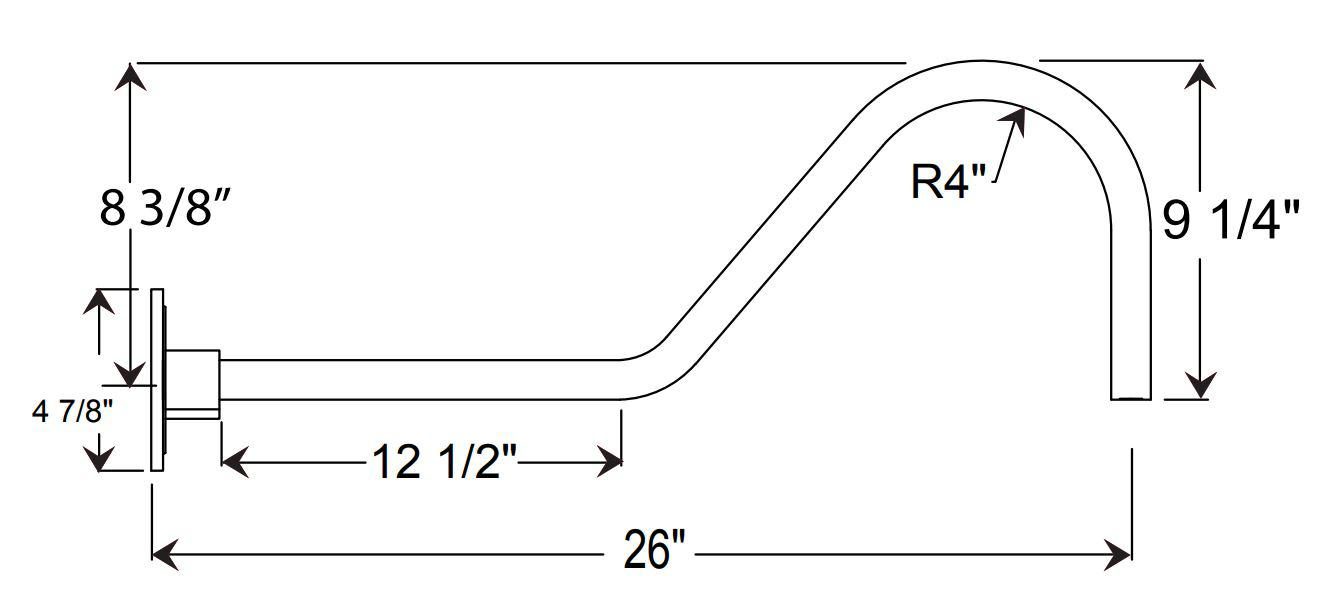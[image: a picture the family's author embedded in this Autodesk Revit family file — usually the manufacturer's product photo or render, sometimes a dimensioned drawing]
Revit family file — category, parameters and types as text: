
# Revit family: MILKCAN T(8,10,12,18)MB
name_source: partatom
category: Lighting Fixtures
units: mm (PartAtom-declared; Revit-internal decimal feet)

## family parameters
Always vertical = Yes
Cut with Voids When Loaded = No
Light Source = Yes
OmniClass Number = 23.80.70.00
OmniClass Title = Lighting
Part Type = Normal
Room Calculation Point = No
Round Connector Dimension = Use Diameter
Shared = No
Work Plane-Based = No

## types (4) — shared parameters
Body Colour = Spun aluminium
Body Material = body
CRI = >90
Color Filter = 16777215
Construction Material = Heavy Duty spun aluminum.
Default Elevation = 0' - 0"
Description = 120-277 Voltage
Dimming = 1%
Dimming Lamp Color Temperature Shift = <None>
Efficiency = 65-125 lumens per watt
Lamp = MB
Life = L70 50,000 hours
Load Classification = Lighting
Manufacturer = ANP Lighting
Photometric Web File = generic.ies
Power Factor = 1
Tilt Angle = 90.00°
URL = https://www.anplighting.com
Voltage = 277 V
Warranty = 5 year limited warranty

## per-type parameters (varying)
| type | Apparent Load | Fixture Diameter | Fixture Height | MCT10 | MCT12 | MCT18 | MCT8 | Wattage Comments | Weight |
| MCT08 | 100 VA | 0' - 8" | 0' - 5" | No | No | No | Yes | 100W Max | 1 lbs |
| MCT10 | 100 VA | 0' - 10" | 0' - 5 1/2" | Yes | No | No | No | 100W Max | 1 lbs |
| MCT12 | 200 VA | 1' - 0" | 0' - 7" | No | Yes | No | No | 200W Max | 1.5 lbs |
| MCT18 | 200 VA | 1' - 6" | 0' - 8 1/2" | No | No | Yes | No | 200W Max | 2 lbs |

note: column(s) folded — value = type name in every type: Model

## geometry (parser evidence)
native form markers: Sweep x42
no freeform markers — native parametric forms only
